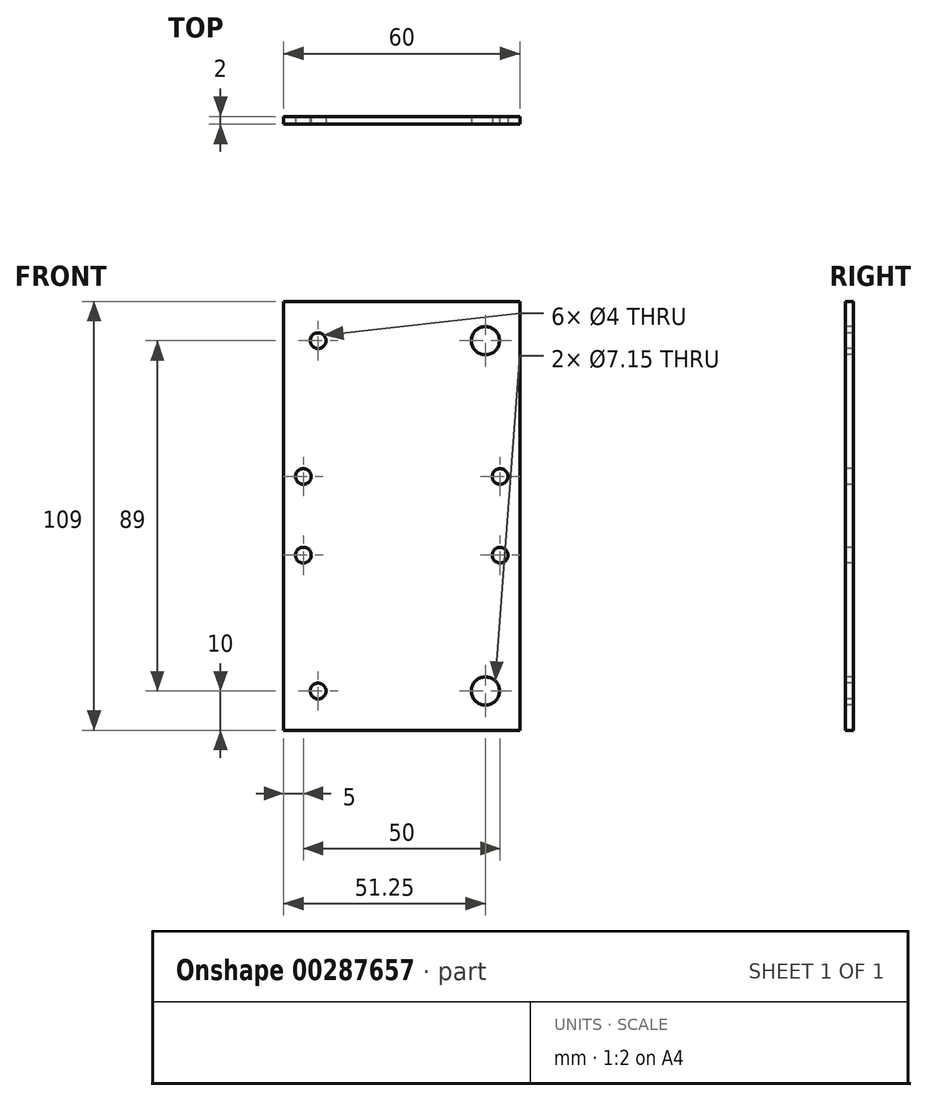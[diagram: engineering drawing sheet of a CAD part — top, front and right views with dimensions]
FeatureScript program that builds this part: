
annotation { "Feature Type Name" : "Feature", "Feature Type Description" : "" }
export const myFeature = defineFeature(function(context is Context, id is Id, definition is map)
    precondition{}
    {
        {
            var Q0;
            Q0=qCreatedBy(makeId("Front.planeOp"),FACE);
            var sketch = newSketch(context, id + "F0", { "sketchPlane" : qUnion([Q0])});
            skLineSegment(sketch, "E0.bottom", {"start": v(30, 54.5) * mm, "end": v(-30, 54.5) * mm});
            skLineSegment(sketch, "E0.top", {"start": v(30, -54.5) * mm, "end": v(-30, -54.5) * mm});
            skLineSegment(sketch, "E0.left", {"start": v(30, 54.5) * mm, "end": v(30, -54.5) * mm});
            skLineSegment(sketch, "E0.right", {"start": v(-30, 54.5) * mm, "end": v(-30, -54.5) * mm});
            skPoint(sketch, "E0.middle", {"position": v(0, 0) * mm});
            skSolve(sketch);
        }
        {
            var Q0;
            Q0 = qSketchRegion(id + "F0", true);
            extrude(context, id + "F1", {"entities" : qUnion([Q0]), "depth" : 2 * mm});
        }
        {
            var Q0;
            Q0=makeQuery(id+"F1.opExtrude","CAP_FACE",FACE,{"disambiguationData":[OSD([sQuery(id+"F0.wireOp",EDGE,"E0.bottom"),sQuery(id+"F0.wireOp",EDGE,"E0.top"),sQuery(id+"F0.wireOp",EDGE,"E0.left"),sQuery(id+"F0.wireOp",EDGE,"E0.right")])],"isStart":false});
            var sketch = newSketch(context, id + "F2", { "sketchPlane" : qUnion([Q0])});
            skLineSegment(sketch, "E1.bottom", {"start": v(21.25, 44.5) * mm, "end": v(-21.25, 44.5) * mm, "construction": true});
            skLineSegment(sketch, "E1.top", {"start": v(21.25, -44.5) * mm, "end": v(-21.25, -44.5) * mm, "construction": true});
            skLineSegment(sketch, "E1.left", {"start": v(21.25, 44.5) * mm, "end": v(21.25, -44.5) * mm, "construction": true});
            skLineSegment(sketch, "E1.right", {"start": v(-21.25, 44.5) * mm, "end": v(-21.25, -44.5) * mm, "construction": true});
            skPoint(sketch, "E1.middle", {"position": v(0, 0) * mm});
            skCircle(sketch, "E2", {"center": v(-21.25, 44.5) * mm, "radius": 2 * mm});
            skCircle(sketch, "E3", {"center": v(-21.25, -44.5) * mm, "radius": 2 * mm});
            skCircle(sketch, "E4", {"center": v(21.25, 44.5) * mm, "radius": 3.58 * mm});
            skCircle(sketch, "E5", {"center": v(21.25, -44.5) * mm, "radius": 3.58 * mm});
            skSolve(sketch);
        }
        {
            var Q0;
            Q0 = qSketchRegion(id + "F2", true);
            extrude(context, id + "F3", {"entities" : qUnion([Q0]), "operationType" : NewBodyOperationType.REMOVE, "endBound" : BoundingType.UP_TO_NEXT, "oppositeDirection" : true, "depth" : 25 * mm});
        }
        {
            var Q0;
            Q0=makeQuery(id+"F1.opExtrude","CAP_FACE",FACE,{"disambiguationData":[OSD([sQuery(id+"F0.wireOp",EDGE,"E0.bottom"),sQuery(id+"F0.wireOp",EDGE,"E0.top"),sQuery(id+"F0.wireOp",EDGE,"E0.left"),sQuery(id+"F0.wireOp",EDGE,"E0.right")])],"isStart":false});
            var sketch = newSketch(context, id + "F4", { "sketchPlane" : qUnion([Q0])});
            skLineSegment(sketch, "E6.bottom", {"start": v(25, -10) * mm, "end": v(-25, -10) * mm, "construction": true});
            skLineSegment(sketch, "E6.top", {"start": v(25, 10) * mm, "end": v(-25, 10) * mm, "construction": true});
            skLineSegment(sketch, "E6.left", {"start": v(25, -10) * mm, "end": v(25, 10) * mm, "construction": true});
            skLineSegment(sketch, "E6.right", {"start": v(-25, -10) * mm, "end": v(-25, 10) * mm, "construction": true});
            skPoint(sketch, "E6.middle", {"position": v(0, 0) * mm});
            skCircle(sketch, "E7", {"center": v(-25, 10) * mm, "radius": 2 * mm});
            skCircle(sketch, "E8", {"center": v(25, 10) * mm, "radius": 2 * mm});
            skCircle(sketch, "E9", {"center": v(-25, -10) * mm, "radius": 2 * mm});
            skCircle(sketch, "E10", {"center": v(25, -10) * mm, "radius": 2 * mm});
            skSolve(sketch);
        }
        {
            var Q0;
            Q0 = qSketchRegion(id + "F4", true);
            extrude(context, id + "F5", {"entities" : qUnion([Q0]), "operationType" : NewBodyOperationType.REMOVE, "endBound" : BoundingType.UP_TO_NEXT, "oppositeDirection" : true, "depth" : 25 * mm});
        }
    });
